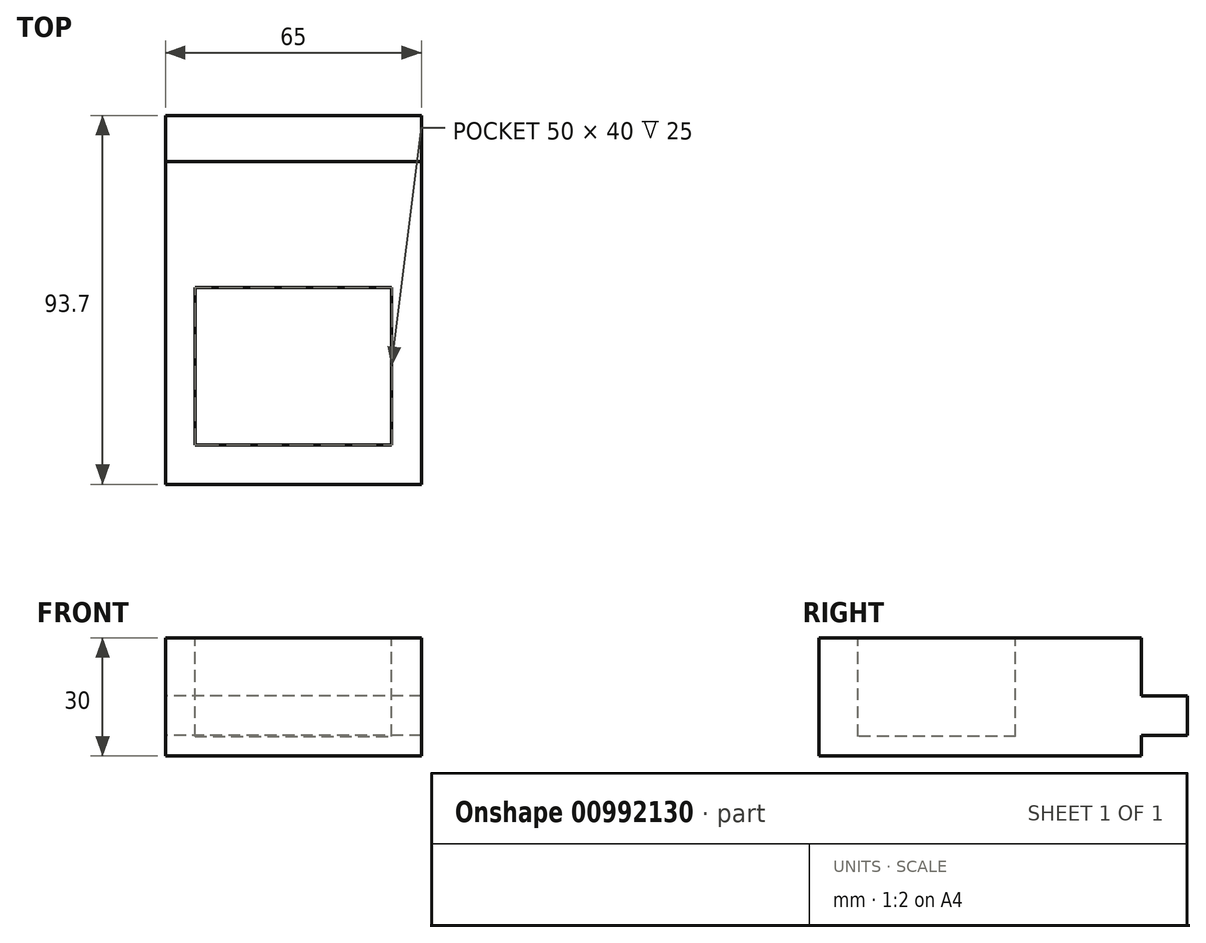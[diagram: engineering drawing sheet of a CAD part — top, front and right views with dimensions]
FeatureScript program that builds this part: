
annotation { "Feature Type Name" : "Feature", "Feature Type Description" : "" }
export const myFeature = defineFeature(function(context is Context, id is Id, definition is map)
    precondition{}
    {
        {
            var Q0;
            Q0=qCreatedBy(makeId("Top.planeOp"),FACE);
            var sketch = newSketch(context, id + "F0", { "sketchPlane" : qUnion([Q0])});
            skLineSegment(sketch, "E0.bottom", {"start": v(-32.5, -46.85) * mm, "end": v(32.5, -46.85) * mm});
            skLineSegment(sketch, "E0.top", {"start": v(-32.5, 46.85) * mm, "end": v(32.5, 46.85) * mm});
            skLineSegment(sketch, "E0.left", {"start": v(-32.5, -46.85) * mm, "end": v(-32.5, 46.85) * mm});
            skLineSegment(sketch, "E0.right", {"start": v(32.5, -46.85) * mm, "end": v(32.5, 46.85) * mm});
            skPoint(sketch, "E0.middle", {"position": v(0, 0) * mm});
            skSolve(sketch);
        }
        {
            var Q0;
            Q0=makeQuery(id+"F0.imprint","IMPRINT",FACE,{"disambiguationData":[TD([[makeQuery(id+"F0.imprint","IMPRINT",EDGE,{"derivedFrom":sQuery(id+"F0.wireOp",EDGE,"E0.bottom")}),1.0]])]});
            extrude(context, id + "F1", {"entities" : qUnion([Q0]), "depth" : 30 * mm, "offsetDistance" : 25 * mm});
        }
        {
            var Q0;
            Q0=makeQuery(id+"F1.opExtrude","SWEPT_FACE",FACE,{"disambiguationData":[OSD([sQuery(id+"F0.wireOp",EDGE,"E0.top")])]});
            var sketch = newSketch(context, id + "F2", { "sketchPlane" : qUnion([Q0])});
            skLineSegment(sketch, "E1.bottom", {"start": v(-32.5, 30) * mm, "end": v(32.5, 30) * mm});
            skLineSegment(sketch, "E1.top", {"start": v(-32.5, 15.2) * mm, "end": v(32.5, 15.2) * mm});
            skLineSegment(sketch, "E1.left", {"start": v(-32.5, 30) * mm, "end": v(-32.5, 15.2) * mm});
            skLineSegment(sketch, "E1.right", {"start": v(32.5, 30) * mm, "end": v(32.5, 15.2) * mm});
            skSolve(sketch);
        }
        {
            var Q0;
            Q0=makeQuery(id+"F2.imprint","IMPRINT",FACE,{"disambiguationData":[TD([[makeQuery(id+"F2.imprint","IMPRINT",EDGE,{"derivedFrom":sQuery(id+"F2.wireOp",EDGE,"E1.bottom")}),1.0]])]});
            extrude(context, id + "F3", {"entities" : qUnion([Q0]), "operationType" : NewBodyOperationType.REMOVE, "oppositeDirection" : true, "depth" : 11.7 * mm, "offsetDistance" : 25 * mm});
        }
        {
            var Q0;
            Q0=makeQuery(id+"F1.opExtrude","SWEPT_FACE",FACE,{"disambiguationData":[OSD([sQuery(id+"F0.wireOp",EDGE,"E0.top")])]});
            var sketch = newSketch(context, id + "F4", { "sketchPlane" : qUnion([Q0])});
            skLineSegment(sketch, "E2.bottom", {"start": v(-32.5, 0) * mm, "end": v(32.5, 0) * mm});
            skLineSegment(sketch, "E2.top", {"start": v(-32.5, 5.2) * mm, "end": v(32.5, 5.2) * mm});
            skLineSegment(sketch, "E2.left", {"start": v(-32.5, 0) * mm, "end": v(-32.5, 5.2) * mm});
            skLineSegment(sketch, "E2.right", {"start": v(32.5, 0) * mm, "end": v(32.5, 5.2) * mm});
            skSolve(sketch);
        }
        {
            var Q0;
            Q0 = qSketchRegion(id + "F4", true);
            extrude(context, id + "F5", {"entities" : qUnion([Q0]), "operationType" : NewBodyOperationType.REMOVE, "oppositeDirection" : true, "depth" : 11.7 * mm, "offsetDistance" : 25 * mm});
        }
        {
            var Q0;
            Q0=makeQuery(id+"F1.opExtrude","CAP_FACE",FACE,{"disambiguationData":[OSD([sQuery(id+"F0.wireOp",EDGE,"E0.bottom"),sQuery(id+"F0.wireOp",EDGE,"E0.top"),sQuery(id+"F0.wireOp",EDGE,"E0.left"),sQuery(id+"F0.wireOp",EDGE,"E0.right")])],"isStart":false});
            var sketch = newSketch(context, id + "F6", { "sketchPlane" : qUnion([Q0])});
            skLineSegment(sketch, "E3.bottom", {"start": v(-25, 3.15) * mm, "end": v(25, 3.15) * mm});
            skLineSegment(sketch, "E3.top", {"start": v(-25, -36.85) * mm, "end": v(25, -36.85) * mm});
            skLineSegment(sketch, "E3.left", {"start": v(-25, 3.15) * mm, "end": v(-25, -36.85) * mm});
            skLineSegment(sketch, "E3.right", {"start": v(25, 3.15) * mm, "end": v(25, -36.85) * mm});
            skPoint(sketch, "E3.middle", {"position": v(0, -16.85) * mm});
            skSolve(sketch);
        }
        {
            var Q0;
            Q0=makeQuery(id+"F6.imprint","IMPRINT",FACE,{"disambiguationData":[TD([[makeQuery(id+"F6.imprint","IMPRINT",EDGE,{"derivedFrom":sQuery(id+"F6.wireOp",EDGE,"E3.bottom")}),-1.0]])]});
            extrude(context, id + "F7", {"entities" : qUnion([Q0]), "operationType" : NewBodyOperationType.REMOVE, "oppositeDirection" : true, "depth" : 25 * mm, "offsetDistance" : 25 * mm});
        }
    });
